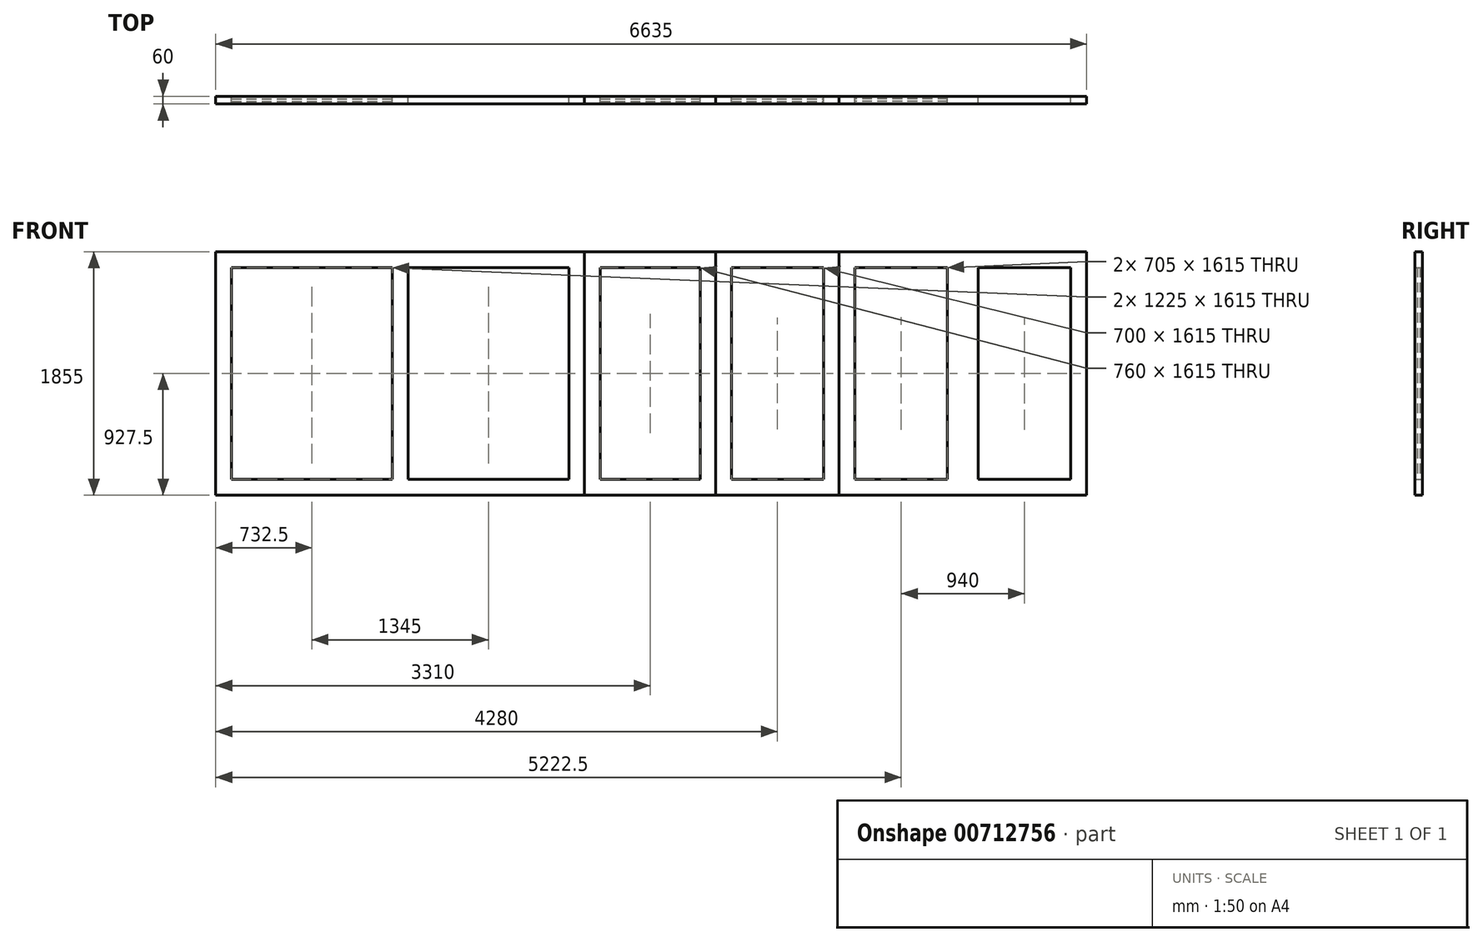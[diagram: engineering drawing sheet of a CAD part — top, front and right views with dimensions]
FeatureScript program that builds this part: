
annotation { "Feature Type Name" : "Feature", "Feature Type Description" : "" }
export const myFeature = defineFeature(function(context is Context, id is Id, definition is map)
    precondition{}
    {
        {
            var Q0;
            Q0=qCreatedBy(makeId("Front.planeOp"),FACE);
            var sketch = newSketch(context, id + "F0", { "sketchPlane" : qUnion([Q0])});
            skLineSegment(sketch, "E0", {"start": v(0, 0) * mm, "end": v(2810, 0) * mm});
            skLineSegment(sketch, "E1", {"start": v(0, 1855) * mm, "end": v(2810, 1855) * mm});
            skLineSegment(sketch, "E2", {"start": v(0, 1855) * mm, "end": v(0, 0) * mm});
            skLineSegment(sketch, "E3", {"start": v(2810, 1855) * mm, "end": v(2810, 0) * mm});
            skLineSegment(sketch, "E4", {"start": v(3810, 1855) * mm, "end": v(3810, 0) * mm});
            skLineSegment(sketch, "E5", {"start": v(4750, 1855) * mm, "end": v(4750, 0) * mm});
            skLineSegment(sketch, "E6", {"start": v(2810, 1855) * mm, "end": v(3810, 1855) * mm});
            skLineSegment(sketch, "E7", {"start": v(3810, 1855) * mm, "end": v(4750, 1855) * mm});
            skLineSegment(sketch, "E8", {"start": v(2810, 0) * mm, "end": v(3810, 0) * mm});
            skLineSegment(sketch, "E9", {"start": v(3810, 0) * mm, "end": v(4750, 0) * mm});
            skLineSegment(sketch, "E10.0", {"start": v(120, 1735) * mm, "end": v(2690, 1735) * mm});
            skLineSegment(sketch, "E10.1", {"start": v(120, 1735) * mm, "end": v(120, 120) * mm});
            skLineSegment(sketch, "E10.2", {"start": v(120, 120) * mm, "end": v(2690, 120) * mm});
            skLineSegment(sketch, "E10.3", {"start": v(2690, 1735) * mm, "end": v(2690, 120) * mm});
            skLineSegment(sketch, "E11.0", {"start": v(2930, 1735) * mm, "end": v(3690, 1735) * mm});
            skLineSegment(sketch, "E11.1", {"start": v(2930, 1735) * mm, "end": v(2930, 120) * mm});
            skLineSegment(sketch, "E11.2", {"start": v(2930, 120) * mm, "end": v(3690, 120) * mm});
            skLineSegment(sketch, "E11.3", {"start": v(3690, 1735) * mm, "end": v(3690, 120) * mm});
            skLineSegment(sketch, "E12.0", {"start": v(3930, 1735) * mm, "end": v(4630, 1735) * mm});
            skLineSegment(sketch, "E12.1", {"start": v(3930, 1735) * mm, "end": v(3930, 120) * mm});
            skLineSegment(sketch, "E12.2", {"start": v(3930, 120) * mm, "end": v(4630, 120) * mm});
            skLineSegment(sketch, "E12.3", {"start": v(4630, 1735) * mm, "end": v(4630, 120) * mm});
            skLineSegment(sketch, "E13", {"start": v(6635, 1855) * mm, "end": v(4750, 1855) * mm});
            skLineSegment(sketch, "E14", {"start": v(6635, 1855) * mm, "end": v(6635, 0) * mm});
            skLineSegment(sketch, "E15", {"start": v(6635, 0) * mm, "end": v(4750, 0) * mm});
            skLineSegment(sketch, "E16.0", {"start": v(6515, 1735) * mm, "end": v(4870, 1735) * mm});
            skLineSegment(sketch, "E16.1", {"start": v(6515, 1735) * mm, "end": v(6515, 120) * mm});
            skLineSegment(sketch, "E16.2", {"start": v(6515, 120) * mm, "end": v(4870, 120) * mm});
            skLineSegment(sketch, "E16.3", {"start": v(4870, 1735) * mm, "end": v(4870, 120) * mm});
            skLineSegment(sketch, "E17", {"start": v(5692.5, 1735) * mm, "end": v(5692.5, 120) * mm});
            skLineSegment(sketch, "E18", {"start": v(5575, 1735) * mm, "end": v(5575, 120) * mm});
            skLineSegment(sketch, "E19.MirrorCS", {"start": v(5810, 1735) * mm, "end": v(5810, 120) * mm});
            skLineSegment(sketch, "E20", {"start": v(1405, 1735) * mm, "end": v(1405, 825.94) * mm, "construction": true});
            skLineSegment(sketch, "E21", {"start": v(1345, 1735) * mm, "end": v(1345, 120) * mm});
            skLineSegment(sketch, "E22.MirrorCS", {"start": v(1465, 1735) * mm, "end": v(1465, 120) * mm});
            skSolve(sketch);
        }
        {
            var Q0;
            Q0=makeQuery(id+"F0.imprint","IMPRINT",FACE,{"disambiguationData":[TD([[makeQuery(id+"F0.imprint","IMPRINT",EDGE,{"derivedFrom":sQuery(id+"F0.wireOp",EDGE,"E0")}),1.0]])]});
            var Q1;
            {var subQ0=sQuery(id+"F0.wireOp",EDGE,"E21");Q1=makeQuery(id+"F0.imprint","IMPRINT",FACE,{"disambiguationData":[TD([[makeQuery(id+"F0.imprint","IMPRINT",EDGE,{"derivedFrom":subQ0}),1.0]])]});}
            extrude(context, id + "F1", {"entities" : qUnion([Q0, Q1]), "depth" : 60 * mm, "offsetDistance" : 25 * mm, "symmetric" : true});
        }
        {
            var Q0;
            {var subQ0=sQuery(id+"F0.wireOp",EDGE,"E10.1");Q0=makeQuery(id+"F0.imprint","IMPRINT",FACE,{"disambiguationData":[TD([[makeQuery(id+"F0.imprint","IMPRINT",EDGE,{"derivedFrom":subQ0}),1.0]])]});}
            extrude(context, id + "F2", {"entities" : qUnion([Q0]), "depth" : 20 * mm, "offsetDistance" : 25 * mm, "symmetric" : true});
        }
        {
            var Q0;
            Q0=makeQuery(id+"F0.imprint","IMPRINT",FACE,{"disambiguationData":[TD([[makeQuery(id+"F0.imprint","IMPRINT",EDGE,{"derivedFrom":sQuery(id+"F0.wireOp",EDGE,"E3")}),1.0]])]});
            extrude(context, id + "F3", {"entities" : qUnion([Q0]), "depth" : 60 * mm, "offsetDistance" : 25 * mm, "symmetric" : true});
        }
        {
            var Q0;
            Q0=makeQuery(id+"F0.imprint","IMPRINT",FACE,{"disambiguationData":[TD([[makeQuery(id+"F0.imprint","IMPRINT",EDGE,{"derivedFrom":sQuery(id+"F0.wireOp",EDGE,"E11.0")}),-1.0]])]});
            extrude(context, id + "F4", {"entities" : qUnion([Q0]), "depth" : 20 * mm, "offsetDistance" : 25 * mm, "symmetric" : true});
        }
        {
            var Q0;
            Q0=makeQuery(id+"F0.imprint","IMPRINT",FACE,{"disambiguationData":[TD([[makeQuery(id+"F0.imprint","IMPRINT",EDGE,{"derivedFrom":sQuery(id+"F0.wireOp",EDGE,"E4")}),1.0]])]});
            extrude(context, id + "F5", {"entities" : qUnion([Q0]), "depth" : 60 * mm, "offsetDistance" : 25 * mm, "symmetric" : true});
        }
        {
            var Q0;
            Q0=makeQuery(id+"F0.imprint","IMPRINT",FACE,{"disambiguationData":[TD([[makeQuery(id+"F0.imprint","IMPRINT",EDGE,{"derivedFrom":sQuery(id+"F0.wireOp",EDGE,"E12.0")}),-1.0]])]});
            extrude(context, id + "F6", {"entities" : qUnion([Q0]), "depth" : 20 * mm, "offsetDistance" : 25 * mm, "symmetric" : true});
        }
        {
            var Q0;
            Q0=makeQuery(id+"F0.imprint","IMPRINT",FACE,{"disambiguationData":[TD([[makeQuery(id+"F0.imprint","IMPRINT",EDGE,{"derivedFrom":sQuery(id+"F0.wireOp",EDGE,"E5")}),1.0]])]});
            var Q1;
            {var subQ0=sQuery(id+"F0.wireOp",EDGE,"E17");Q1=makeQuery(id+"F0.imprint","IMPRINT",FACE,{"disambiguationData":[TD([[makeQuery(id+"F0.imprint","IMPRINT",EDGE,{"derivedFrom":subQ0}),-1.0]])]});}
            var Q2;
            {var subQ0=sQuery(id+"F0.wireOp",EDGE,"E17");Q2=makeQuery(id+"F0.imprint","IMPRINT",FACE,{"disambiguationData":[TD([[makeQuery(id+"F0.imprint","IMPRINT",EDGE,{"derivedFrom":subQ0}),1.0]])]});}
            extrude(context, id + "F7", {"entities" : qUnion([Q0, Q1, Q2]), "depth" : 60 * mm, "offsetDistance" : 25 * mm, "symmetric" : true});
        }
        {
            var Q0;
            {var subQ0=sQuery(id+"F0.wireOp",EDGE,"E16.3");Q0=makeQuery(id+"F0.imprint","IMPRINT",FACE,{"disambiguationData":[TD([[makeQuery(id+"F0.imprint","IMPRINT",EDGE,{"derivedFrom":subQ0}),1.0]])]});}
            extrude(context, id + "F8", {"entities" : qUnion([Q0]), "depth" : 20 * mm, "offsetDistance" : 25 * mm, "symmetric" : true});
        }
    });
